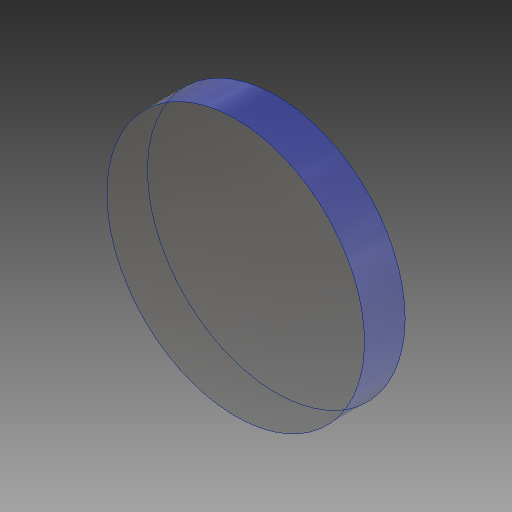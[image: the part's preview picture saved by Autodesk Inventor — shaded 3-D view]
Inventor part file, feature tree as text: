
AUTODESK INVENTOR PART (.ipt)
format: ipt  version: 2017 SP1 (Build 210196100, 196)  size: 96,256 bytes
history: native  units: mm
features: extrude x1, sketch x1
ambient origin geometry x8: Origin, YZ Plane, XZ Plane, XY Plane, X Axis, Y Axis, Z Axis, Center Point
bodies: Solid1 (feature_tree)
feature tree (2):
  extrude  "Extrusion1"  Depth=8.0mm TaperAngle=0.0deg
  sketch  "Sketch1"  dims[d0=50.8mm d1=8.0mm d2=0.0mm]
